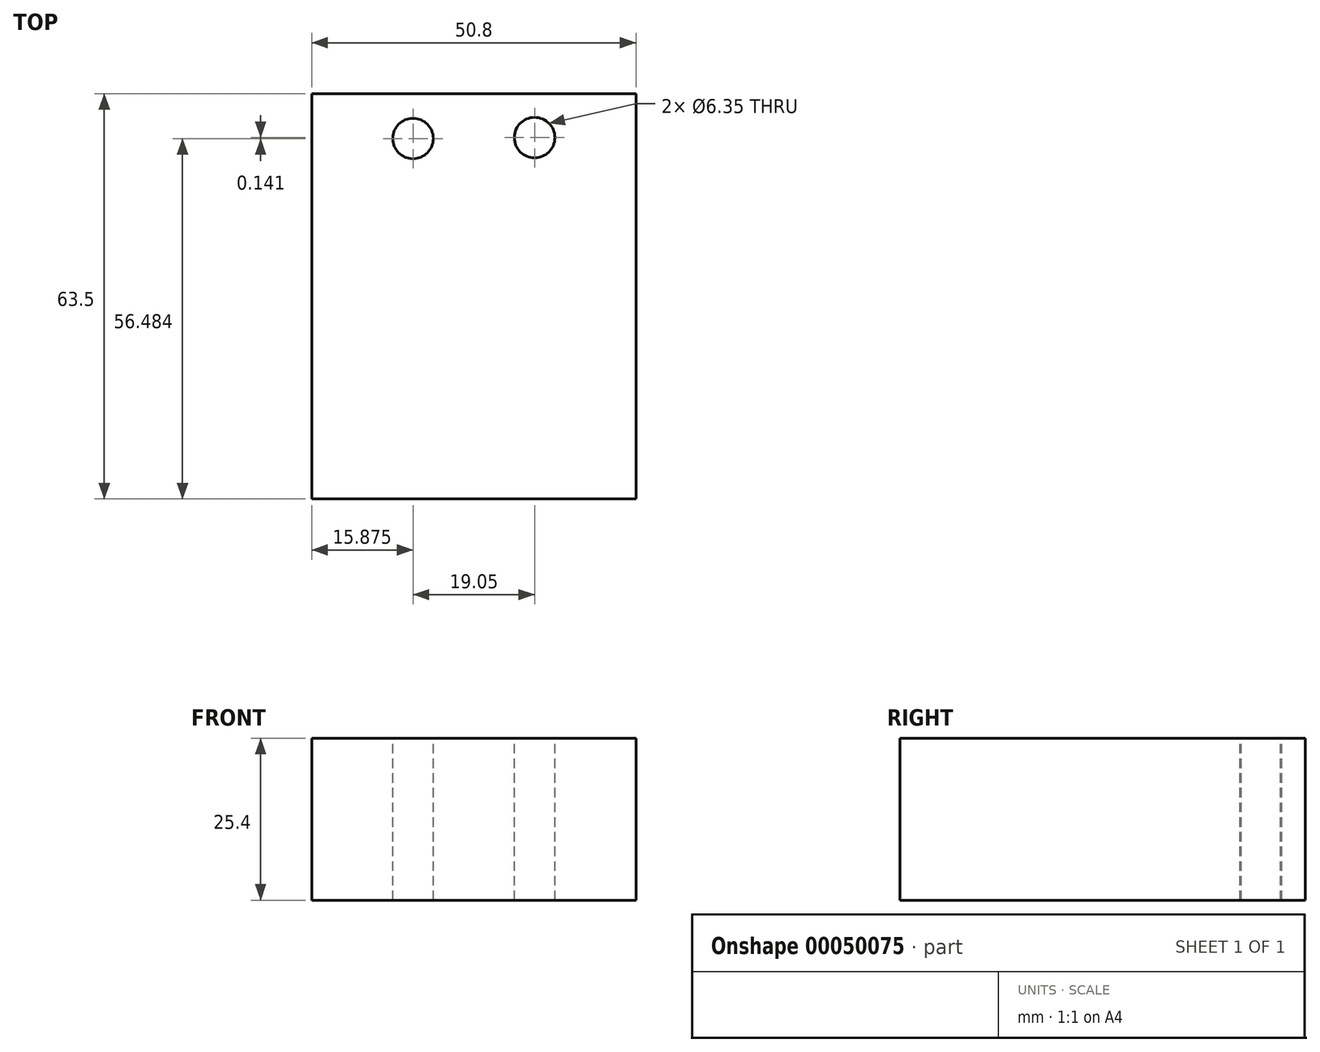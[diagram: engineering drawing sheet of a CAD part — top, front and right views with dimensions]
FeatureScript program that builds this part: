
annotation { "Feature Type Name" : "Feature", "Feature Type Description" : "" }
export const myFeature = defineFeature(function(context is Context, id is Id, definition is map)
    precondition{}
    {
        {
            var Q0;
            Q0=qCreatedBy(makeId("Front.planeOp"),FACE);
            var sketch = newSketch(context, id + "F0", { "sketchPlane" : qUnion([Q0])});
            skLineSegment(sketch, "E0.bottom", {"start": v(0, 0) * mm, "end": v(50.8, 0) * mm});
            skLineSegment(sketch, "E0.top", {"start": v(0, 25.4) * mm, "end": v(50.8, 25.4) * mm});
            skLineSegment(sketch, "E0.left", {"start": v(0, 0) * mm, "end": v(0, 25.4) * mm});
            skLineSegment(sketch, "E0.right", {"start": v(50.8, 0) * mm, "end": v(50.8, 25.4) * mm});
            skSolve(sketch);
        }
        {
            var Q0;
            Q0=makeQuery(id+"F0.imprint","IMPRINT",FACE,{"disambiguationData":[TD([[makeQuery(id+"F0.imprint","IMPRINT",EDGE,{"derivedFrom":sQuery(id+"F0.wireOp",EDGE,"E0.bottom")}),1.0]])]});
            extrude(context, id + "F1", {"entities" : qUnion([Q0]), "depth" : 63.5 * mm});
        }
        {
            var Q0;
            Q0=makeQuery(id+"F1.opExtrude","SWEPT_FACE",FACE,{"disambiguationData":[OSD([sQuery(id+"F0.wireOp",EDGE,"E0.top")])]});
            var sketch = newSketch(context, id + "F2", { "sketchPlane" : qUnion([Q0])});
            skCircle(sketch, "E1", {"center": v(15.88, -7.02) * mm, "radius": 3.18 * mm});
            skCircle(sketch, "E2", {"center": v(34.92, -6.87) * mm, "radius": 3.18 * mm});
            skSolve(sketch);
        }
        {
            var Q0;
            Q0 = qSketchRegion(id + "F2", true);
            extrude(context, id + "F3", {"entities" : qUnion([Q0]), "operationType" : NewBodyOperationType.REMOVE, "oppositeDirection" : true, "depth" : 25.4 * mm});
        }
    });
